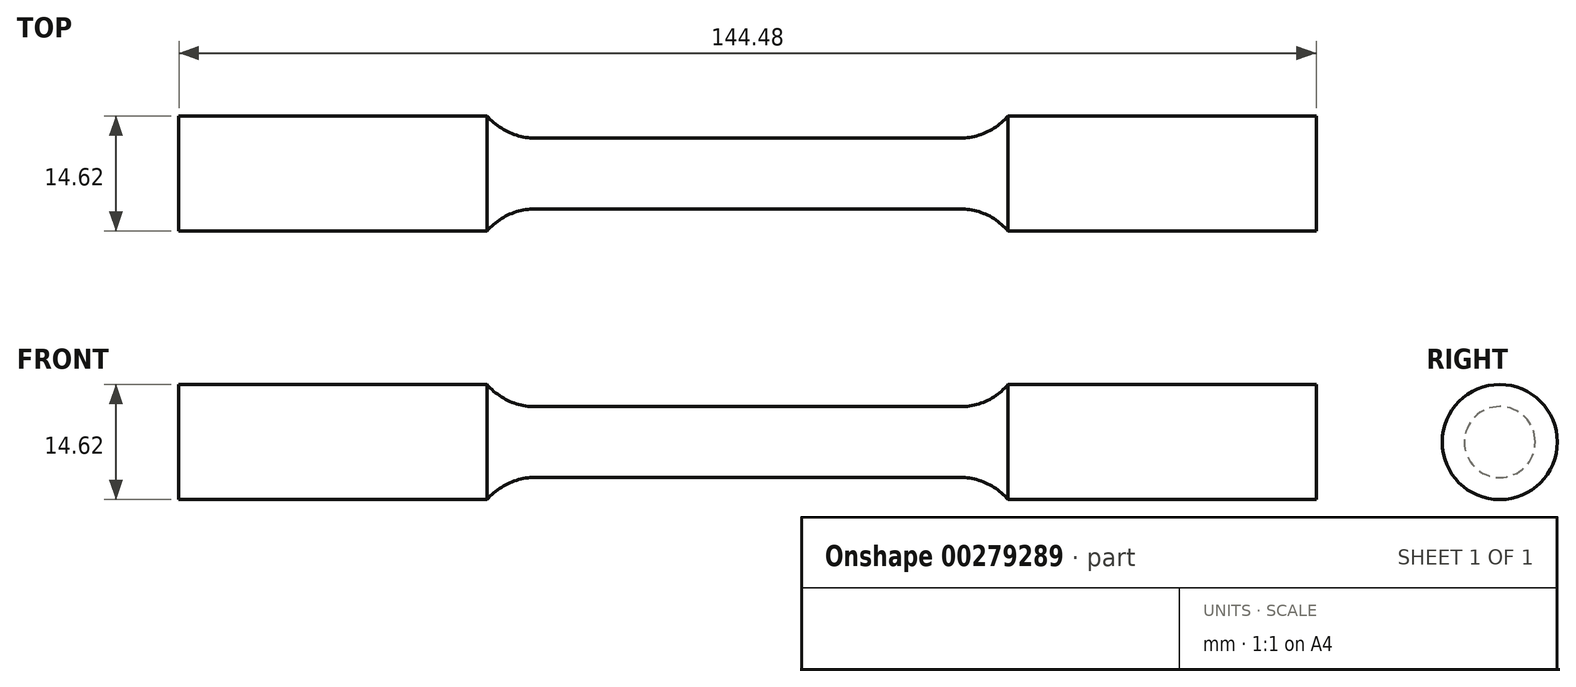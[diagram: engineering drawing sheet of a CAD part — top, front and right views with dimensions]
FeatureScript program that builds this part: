
annotation { "Feature Type Name" : "Feature", "Feature Type Description" : "" }
export const myFeature = defineFeature(function(context is Context, id is Id, definition is map)
    precondition{}
    {
        {
            var Q0;
            Q0=qCreatedBy(makeId("Front.planeOp"),FACE);
            var sketch = newSketch(context, id + "F0", { "sketchPlane" : qUnion([Q0])});
            skLineSegment(sketch, "E0", {"start": v(0, 4.5) * mm, "end": v(27, 4.5) * mm});
            skArc(sketch, "E1", {"start": v(27, 4.5) * mm, "mid": v(30.35, 5.24) * mm, "end": v(33.09, 7.3) * mm});
            skLineSegment(sketch, "E2", {"start": v(33.09, 7.3) * mm, "end": v(72.24, 7.3) * mm});
            skLineSegment(sketch, "E3", {"start": v(72.24, 7.3) * mm, "end": v(72.24, 0) * mm});
            skLineSegment(sketch, "E4.MirrorCS", {"start": v(0, 4.5) * mm, "end": v(-27, 4.5) * mm});
            skLineSegment(sketch, "E5.MirrorCS", {"start": v(-33.09, 7.3) * mm, "end": v(-72.24, 7.3) * mm});
            skArc(sketch, "E6.MirrorCS", {"start": v(-27, 4.5) * mm, "mid": v(-30.35, 5.24) * mm, "end": v(-33.09, 7.3) * mm});
            skLineSegment(sketch, "E7.MirrorCS", {"start": v(-72.24, 7.3) * mm, "end": v(-72.24, 0) * mm});
            skLineSegment(sketch, "E8", {"start": v(-72.24, 0) * mm, "end": v(72.24, 0) * mm});
            skSolve(sketch);
        }
        {
            var Q0;
            Q0 = qSketchRegion(id + "F0", true);
            var Q1;
            Q1=sQuery(id+"F0.wireOp",EDGE,"E8");
            revolve(context, id + "F1", {"entities" : qUnion([Q0]), "axis" : qUnion([Q1]), "revolveType" : RevolveType.FULL});
        }
    });
